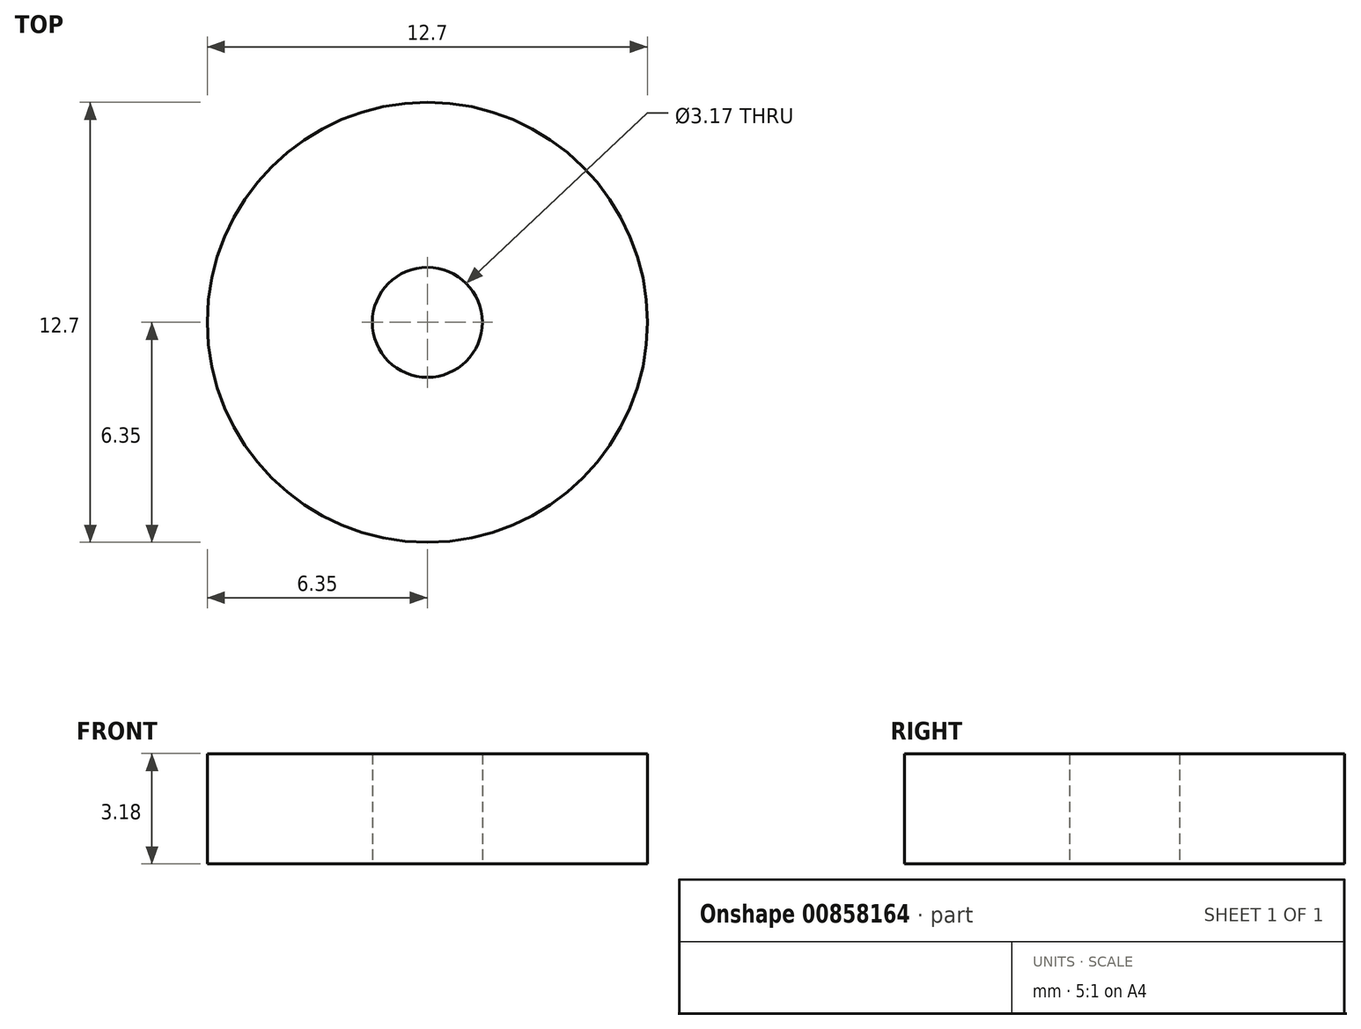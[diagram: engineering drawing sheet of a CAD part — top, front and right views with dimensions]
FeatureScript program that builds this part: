
annotation { "Feature Type Name" : "Feature", "Feature Type Description" : "" }
export const myFeature = defineFeature(function(context is Context, id is Id, definition is map)
    precondition{}
    {
        {
            var Q0;
            Q0=qCreatedBy(makeId("Top.planeOp"),FACE);
            var sketch = newSketch(context, id + "F0", { "sketchPlane" : qUnion([Q0])});
            skCircle(sketch, "E0", {"center": v(0, 0) * mm, "radius": 6.35 * mm});
            skCircle(sketch, "E1", {"center": v(0, 0) * mm, "radius": 1.59 * mm});
            skSolve(sketch);
        }
        {
            var Q0;
            Q0 = qSketchRegion(id + "F0", true);
            extrude(context, id + "F1", {"entities" : qUnion([Q0]), "depth" : 3.17 * mm, "offsetDistance" : 25.4 * mm});
        }
    });
